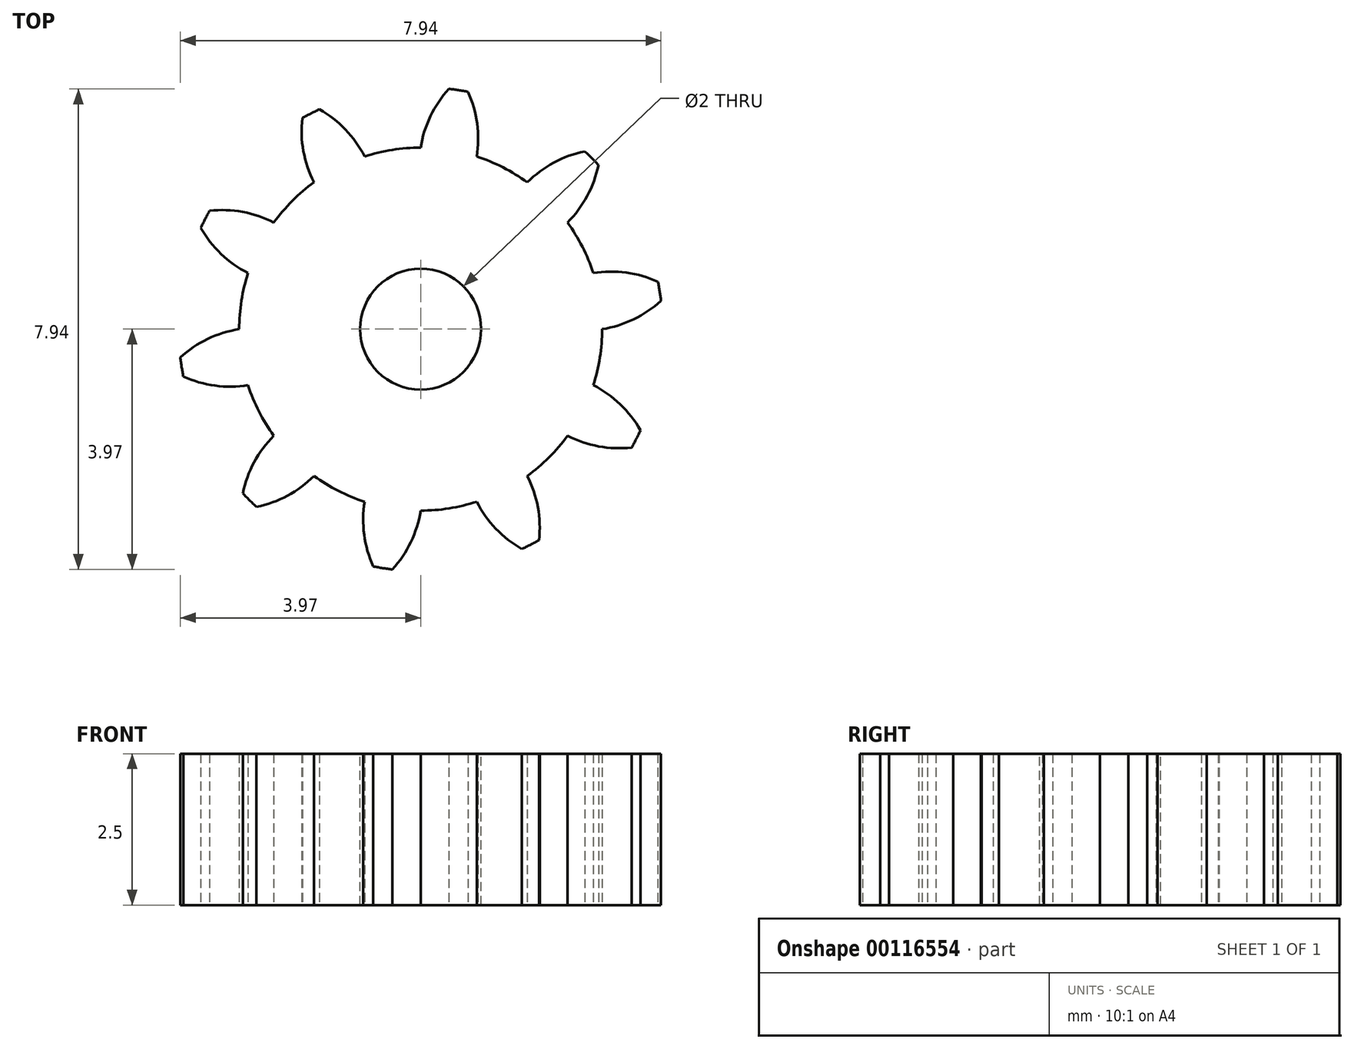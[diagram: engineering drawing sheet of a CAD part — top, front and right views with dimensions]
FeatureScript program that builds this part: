
annotation { "Feature Type Name" : "Feature", "Feature Type Description" : "" }
export const myFeature = defineFeature(function(context is Context, id is Id, definition is map)
    precondition{}
    {
        {
            var Q0;
            Q0=qCreatedBy(makeId("Top.planeOp"),FACE);
            var sketch = newSketch(context, id + "F0", { "sketchPlane" : qUnion([Q0])});
            skCircle(sketch, "E0", {"center": v(0, 0) * mm, "radius": 4 * mm, "construction": true});
            skCircle(sketch, "E1", {"center": v(0, 0) * mm, "radius": 3 * mm, "construction": true});
            skLineSegment(sketch, "E2", {"start": v(0, 0) * mm, "end": v(4.1, 0) * mm, "construction": true});
            skLineSegment(sketch, "E3", {"start": v(0, 0) * mm, "end": v(3.9, 1.27) * mm, "construction": true});
            skLineSegment(sketch, "E4", {"start": v(0, 0) * mm, "end": v(3.48, 2.53) * mm, "construction": true});
            skLineSegment(sketch, "E5", {"start": v(0, 0) * mm, "end": v(4.3, 0.68) * mm, "construction": true});
            skArc(sketch, "E6", {"start": v(2.43, 1.76) * mm, "mid": v(2.67, 1.36) * mm, "end": v(2.85, 0.93) * mm});
            skArc(sketch, "E7", {"start": v(3.92, 0.78) * mm, "mid": v(3.4, 0.93) * mm, "end": v(2.85, 0.93) * mm});
            skArc(sketch, "E8", {"start": v(3.92, 0.78) * mm, "mid": v(3.94, 0.7) * mm, "end": v(3.95, 0.63) * mm});
            skArc(sketch, "E9.MirrorCS", {"start": v(3.97, 0.47) * mm, "mid": v(3.52, 0.16) * mm, "end": v(3, 0) * mm});
            skArc(sketch, "E10.MirrorCS", {"start": v(3.97, 0.47) * mm, "mid": v(3.96, 0.55) * mm, "end": v(3.95, 0.63) * mm});
            skArc(sketch, "E11.1.0", {"start": v(0.93, 2.85) * mm, "mid": v(1.36, 2.67) * mm, "end": v(1.76, 2.43) * mm});
            skArc(sketch, "E11.1.1", {"start": v(2.71, 2.94) * mm, "mid": v(2.2, 2.75) * mm, "end": v(1.76, 2.43) * mm});
            skArc(sketch, "E11.1.2", {"start": v(2.71, 2.94) * mm, "mid": v(2.77, 2.88) * mm, "end": v(2.83, 2.83) * mm});
            skArc(sketch, "E11.1.3", {"start": v(2.94, 2.71) * mm, "mid": v(2.88, 2.77) * mm, "end": v(2.83, 2.83) * mm});
            skArc(sketch, "E11.1.4", {"start": v(2.94, 2.71) * mm, "mid": v(2.75, 2.2) * mm, "end": v(2.43, 1.76) * mm});
            skArc(sketch, "E11.2.0", {"start": v(-0.93, 2.85) * mm, "mid": v(-0.47, 2.96) * mm, "end": v(0, 3) * mm});
            skArc(sketch, "E11.2.1", {"start": v(0.47, 3.97) * mm, "mid": v(0.16, 3.52) * mm, "end": v(0, 3) * mm});
            skArc(sketch, "E11.2.2", {"start": v(0.47, 3.97) * mm, "mid": v(0.55, 3.96) * mm, "end": v(0.63, 3.95) * mm});
            skArc(sketch, "E11.2.3", {"start": v(0.78, 3.92) * mm, "mid": v(0.7, 3.94) * mm, "end": v(0.63, 3.95) * mm});
            skArc(sketch, "E11.2.4", {"start": v(0.78, 3.92) * mm, "mid": v(0.93, 3.4) * mm, "end": v(0.93, 2.85) * mm});
            skArc(sketch, "E11.3.0", {"start": v(-2.43, 1.76) * mm, "mid": v(-2.12, 2.12) * mm, "end": v(-1.76, 2.43) * mm});
            skArc(sketch, "E11.3.1", {"start": v(-1.96, 3.49) * mm, "mid": v(-1.94, 2.94) * mm, "end": v(-1.76, 2.43) * mm});
            skArc(sketch, "E11.3.2", {"start": v(-1.96, 3.49) * mm, "mid": v(-1.89, 3.53) * mm, "end": v(-1.82, 3.56) * mm});
            skArc(sketch, "E11.3.3", {"start": v(-1.67, 3.63) * mm, "mid": v(-1.74, 3.6) * mm, "end": v(-1.82, 3.56) * mm});
            skArc(sketch, "E11.3.4", {"start": v(-1.67, 3.63) * mm, "mid": v(-1.24, 3.3) * mm, "end": v(-0.93, 2.85) * mm});
            skArc(sketch, "E11.4.0", {"start": v(-3, 0) * mm, "mid": v(-2.96, 0.47) * mm, "end": v(-2.85, 0.93) * mm});
            skArc(sketch, "E11.4.1", {"start": v(-3.63, 1.67) * mm, "mid": v(-3.3, 1.24) * mm, "end": v(-2.85, 0.93) * mm});
            skArc(sketch, "E11.4.2", {"start": v(-3.63, 1.67) * mm, "mid": v(-3.6, 1.74) * mm, "end": v(-3.56, 1.82) * mm});
            skArc(sketch, "E11.4.3", {"start": v(-3.49, 1.96) * mm, "mid": v(-3.53, 1.89) * mm, "end": v(-3.56, 1.82) * mm});
            skArc(sketch, "E11.4.4", {"start": v(-3.49, 1.96) * mm, "mid": v(-2.94, 1.94) * mm, "end": v(-2.43, 1.76) * mm});
            skArc(sketch, "E11.5.0", {"start": v(-2.43, -1.76) * mm, "mid": v(-2.67, -1.36) * mm, "end": v(-2.85, -0.93) * mm});
            skArc(sketch, "E11.5.1", {"start": v(-3.92, -0.78) * mm, "mid": v(-3.4, -0.93) * mm, "end": v(-2.85, -0.93) * mm});
            skArc(sketch, "E11.5.2", {"start": v(-3.92, -0.78) * mm, "mid": v(-3.94, -0.7) * mm, "end": v(-3.95, -0.63) * mm});
            skArc(sketch, "E11.5.3", {"start": v(-3.97, -0.47) * mm, "mid": v(-3.96, -0.55) * mm, "end": v(-3.95, -0.63) * mm});
            skArc(sketch, "E11.5.4", {"start": v(-3.97, -0.47) * mm, "mid": v(-3.52, -0.16) * mm, "end": v(-3, 0) * mm});
            skArc(sketch, "E11.6.0", {"start": v(-0.93, -2.85) * mm, "mid": v(-1.36, -2.67) * mm, "end": v(-1.76, -2.43) * mm});
            skArc(sketch, "E11.6.1", {"start": v(-2.71, -2.94) * mm, "mid": v(-2.2, -2.75) * mm, "end": v(-1.76, -2.43) * mm});
            skArc(sketch, "E11.6.2", {"start": v(-2.71, -2.94) * mm, "mid": v(-2.77, -2.88) * mm, "end": v(-2.83, -2.83) * mm});
            skArc(sketch, "E11.6.3", {"start": v(-2.94, -2.71) * mm, "mid": v(-2.88, -2.77) * mm, "end": v(-2.83, -2.83) * mm});
            skArc(sketch, "E11.6.4", {"start": v(-2.94, -2.71) * mm, "mid": v(-2.75, -2.2) * mm, "end": v(-2.43, -1.76) * mm});
            skArc(sketch, "E11.7.0", {"start": v(0.93, -2.85) * mm, "mid": v(0.47, -2.96) * mm, "end": v(0, -3) * mm});
            skArc(sketch, "E11.7.1", {"start": v(-0.47, -3.97) * mm, "mid": v(-0.16, -3.52) * mm, "end": v(0, -3) * mm});
            skArc(sketch, "E11.7.2", {"start": v(-0.47, -3.97) * mm, "mid": v(-0.55, -3.96) * mm, "end": v(-0.63, -3.95) * mm});
            skArc(sketch, "E11.7.3", {"start": v(-0.78, -3.92) * mm, "mid": v(-0.7, -3.94) * mm, "end": v(-0.63, -3.95) * mm});
            skArc(sketch, "E11.7.4", {"start": v(-0.78, -3.92) * mm, "mid": v(-0.93, -3.4) * mm, "end": v(-0.93, -2.85) * mm});
            skArc(sketch, "E11.8.0", {"start": v(2.43, -1.76) * mm, "mid": v(2.12, -2.12) * mm, "end": v(1.76, -2.43) * mm});
            skArc(sketch, "E11.8.1", {"start": v(1.96, -3.49) * mm, "mid": v(1.94, -2.94) * mm, "end": v(1.76, -2.43) * mm});
            skArc(sketch, "E11.8.2", {"start": v(1.96, -3.49) * mm, "mid": v(1.89, -3.53) * mm, "end": v(1.82, -3.56) * mm});
            skArc(sketch, "E11.8.3", {"start": v(1.67, -3.63) * mm, "mid": v(1.74, -3.6) * mm, "end": v(1.82, -3.56) * mm});
            skArc(sketch, "E11.8.4", {"start": v(1.67, -3.63) * mm, "mid": v(1.24, -3.3) * mm, "end": v(0.93, -2.85) * mm});
            skArc(sketch, "E11.9.0", {"start": v(3, 0) * mm, "mid": v(2.96, -0.47) * mm, "end": v(2.85, -0.93) * mm});
            skArc(sketch, "E11.9.1", {"start": v(3.63, -1.67) * mm, "mid": v(3.3, -1.24) * mm, "end": v(2.85, -0.93) * mm});
            skArc(sketch, "E11.9.2", {"start": v(3.63, -1.67) * mm, "mid": v(3.6, -1.74) * mm, "end": v(3.56, -1.82) * mm});
            skArc(sketch, "E11.9.3", {"start": v(3.49, -1.96) * mm, "mid": v(3.53, -1.89) * mm, "end": v(3.56, -1.82) * mm});
            skArc(sketch, "E11.9.4", {"start": v(3.49, -1.96) * mm, "mid": v(2.94, -1.94) * mm, "end": v(2.43, -1.76) * mm});
            skSolve(sketch);
        }
        {
            var Q0;
            Q0 = qSketchRegion(id + "F0", true);
            extrude(context, id + "F1", {"entities" : qUnion([Q0]), "depth" : 2.5 * mm});
        }
        {
            var Q0;
            Q0=makeQuery(id+"F1.opExtrude","CAP_FACE",FACE,{"disambiguationData":[OSD([sQuery(id+"F0.wireOp",EDGE,"E6"),sQuery(id+"F0.wireOp",EDGE,"E7"),sQuery(id+"F0.wireOp",EDGE,"E8"),sQuery(id+"F0.wireOp",EDGE,"E9.MirrorCS"),sQuery(id+"F0.wireOp",EDGE,"E10.MirrorCS"),sQuery(id+"F0.wireOp",EDGE,"E11.1.0"),sQuery(id+"F0.wireOp",EDGE,"E11.1.1"),sQuery(id+"F0.wireOp",EDGE,"E11.1.2"),sQuery(id+"F0.wireOp",EDGE,"E11.1.3"),sQuery(id+"F0.wireOp",EDGE,"E11.1.4"),sQuery(id+"F0.wireOp",EDGE,"E11.2.0"),sQuery(id+"F0.wireOp",EDGE,"E11.2.1"),sQuery(id+"F0.wireOp",EDGE,"E11.2.2"),sQuery(id+"F0.wireOp",EDGE,"E11.2.3"),sQuery(id+"F0.wireOp",EDGE,"E11.2.4"),sQuery(id+"F0.wireOp",EDGE,"E11.3.0"),sQuery(id+"F0.wireOp",EDGE,"E11.3.1"),sQuery(id+"F0.wireOp",EDGE,"E11.3.2"),sQuery(id+"F0.wireOp",EDGE,"E11.3.3"),sQuery(id+"F0.wireOp",EDGE,"E11.3.4"),sQuery(id+"F0.wireOp",EDGE,"E11.4.0"),sQuery(id+"F0.wireOp",EDGE,"E11.4.1"),sQuery(id+"F0.wireOp",EDGE,"E11.4.2"),sQuery(id+"F0.wireOp",EDGE,"E11.4.3"),sQuery(id+"F0.wireOp",EDGE,"E11.4.4"),sQuery(id+"F0.wireOp",EDGE,"E11.5.0"),sQuery(id+"F0.wireOp",EDGE,"E11.5.1"),sQuery(id+"F0.wireOp",EDGE,"E11.5.2"),sQuery(id+"F0.wireOp",EDGE,"E11.5.3"),sQuery(id+"F0.wireOp",EDGE,"E11.5.4"),sQuery(id+"F0.wireOp",EDGE,"E11.6.0"),sQuery(id+"F0.wireOp",EDGE,"E11.6.1"),sQuery(id+"F0.wireOp",EDGE,"E11.6.2"),sQuery(id+"F0.wireOp",EDGE,"E11.6.3"),sQuery(id+"F0.wireOp",EDGE,"E11.6.4"),sQuery(id+"F0.wireOp",EDGE,"E11.7.0"),sQuery(id+"F0.wireOp",EDGE,"E11.7.1"),sQuery(id+"F0.wireOp",EDGE,"E11.7.2"),sQuery(id+"F0.wireOp",EDGE,"E11.7.3"),sQuery(id+"F0.wireOp",EDGE,"E11.7.4"),sQuery(id+"F0.wireOp",EDGE,"E11.8.0"),sQuery(id+"F0.wireOp",EDGE,"E11.8.1"),sQuery(id+"F0.wireOp",EDGE,"E11.8.2"),sQuery(id+"F0.wireOp",EDGE,"E11.8.3"),sQuery(id+"F0.wireOp",EDGE,"E11.8.4"),sQuery(id+"F0.wireOp",EDGE,"E11.9.0"),sQuery(id+"F0.wireOp",EDGE,"E11.9.1"),sQuery(id+"F0.wireOp",EDGE,"E11.9.2"),sQuery(id+"F0.wireOp",EDGE,"E11.9.3"),sQuery(id+"F0.wireOp",EDGE,"E11.9.4")])],"isStart":false});
            var sketch = newSketch(context, id + "F2", { "sketchPlane" : qUnion([Q0])});
            skCircle(sketch, "E12", {"center": v(0, 0) * mm, "radius": 1 * mm});
            skSolve(sketch);
        }
        {
            var Q0;
            Q0 = qSketchRegion(id + "F2", true);
            extrude(context, id + "F3", {"entities" : qUnion([Q0]), "operationType" : NewBodyOperationType.REMOVE, "endBound" : BoundingType.THROUGH_ALL, "oppositeDirection" : true, "depth" : 25 * mm});
        }
    });
